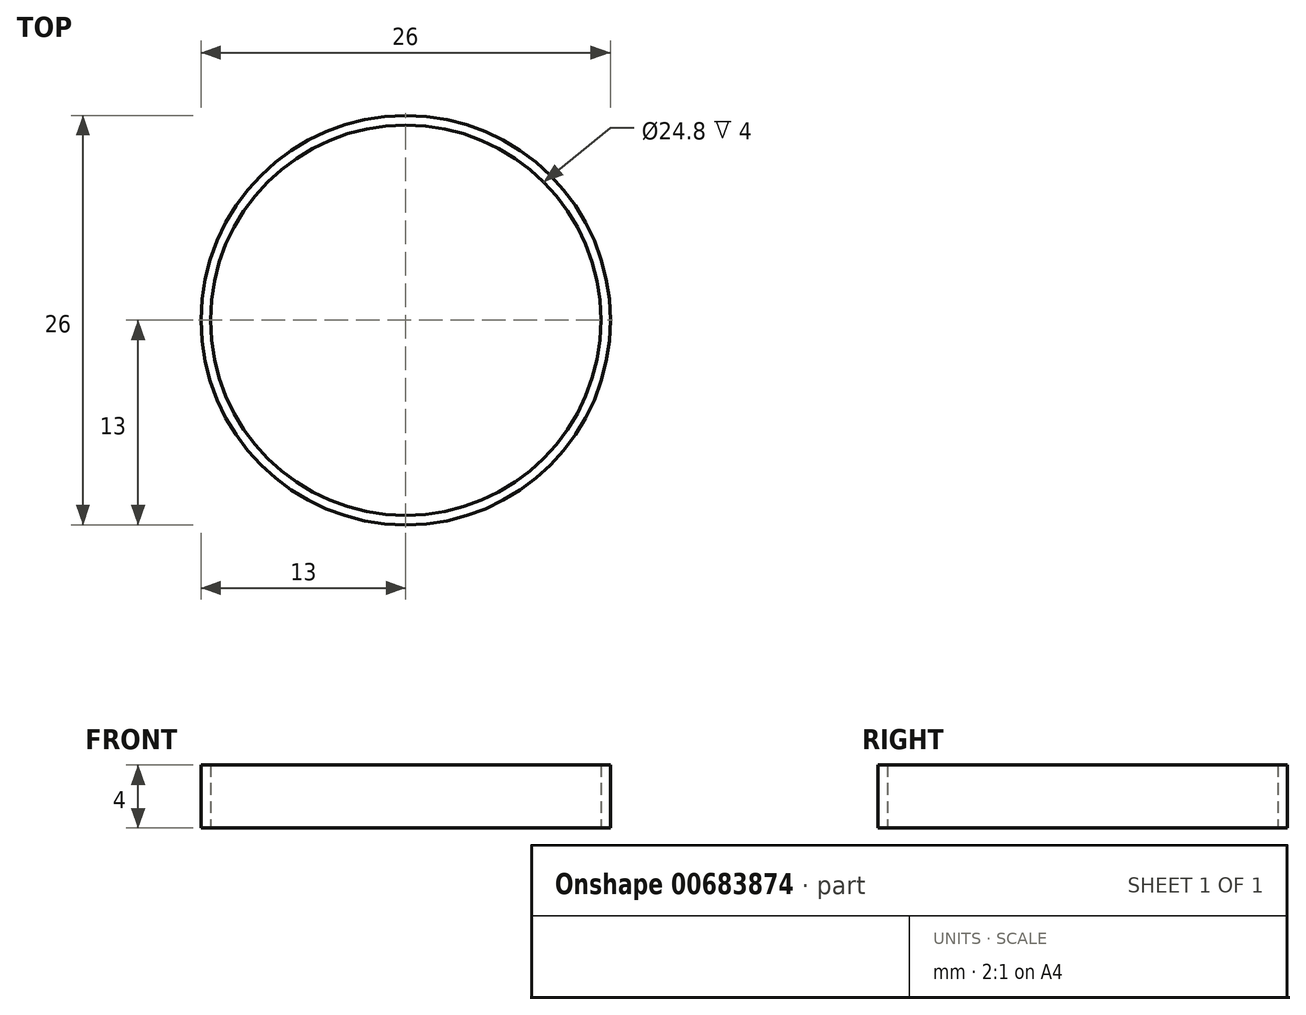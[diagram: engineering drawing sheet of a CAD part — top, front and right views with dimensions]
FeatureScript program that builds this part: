
annotation { "Feature Type Name" : "Feature", "Feature Type Description" : "" }
export const myFeature = defineFeature(function(context is Context, id is Id, definition is map)
    precondition{}
    {
        {
            var Q0;
            Q0=qCreatedBy(makeId("Top.planeOp"),FACE);
            var sketch = newSketch(context, id + "F0", { "sketchPlane" : qUnion([Q0])});
            skCircle(sketch, "E0", {"center": v(0, 0) * mm, "radius": 13 * mm});
            skCircle(sketch, "E1", {"center": v(0, 0) * mm, "radius": 12.4 * mm});
            skSolve(sketch);
        }
        {
            var Q0;
            Q0 = qSketchRegion(id + "F0", true);
            extrude(context, id + "F1", {"entities" : qUnion([Q0]), "depth" : 4 * mm, "offsetDistance" : 25 * mm});
        }
    });
